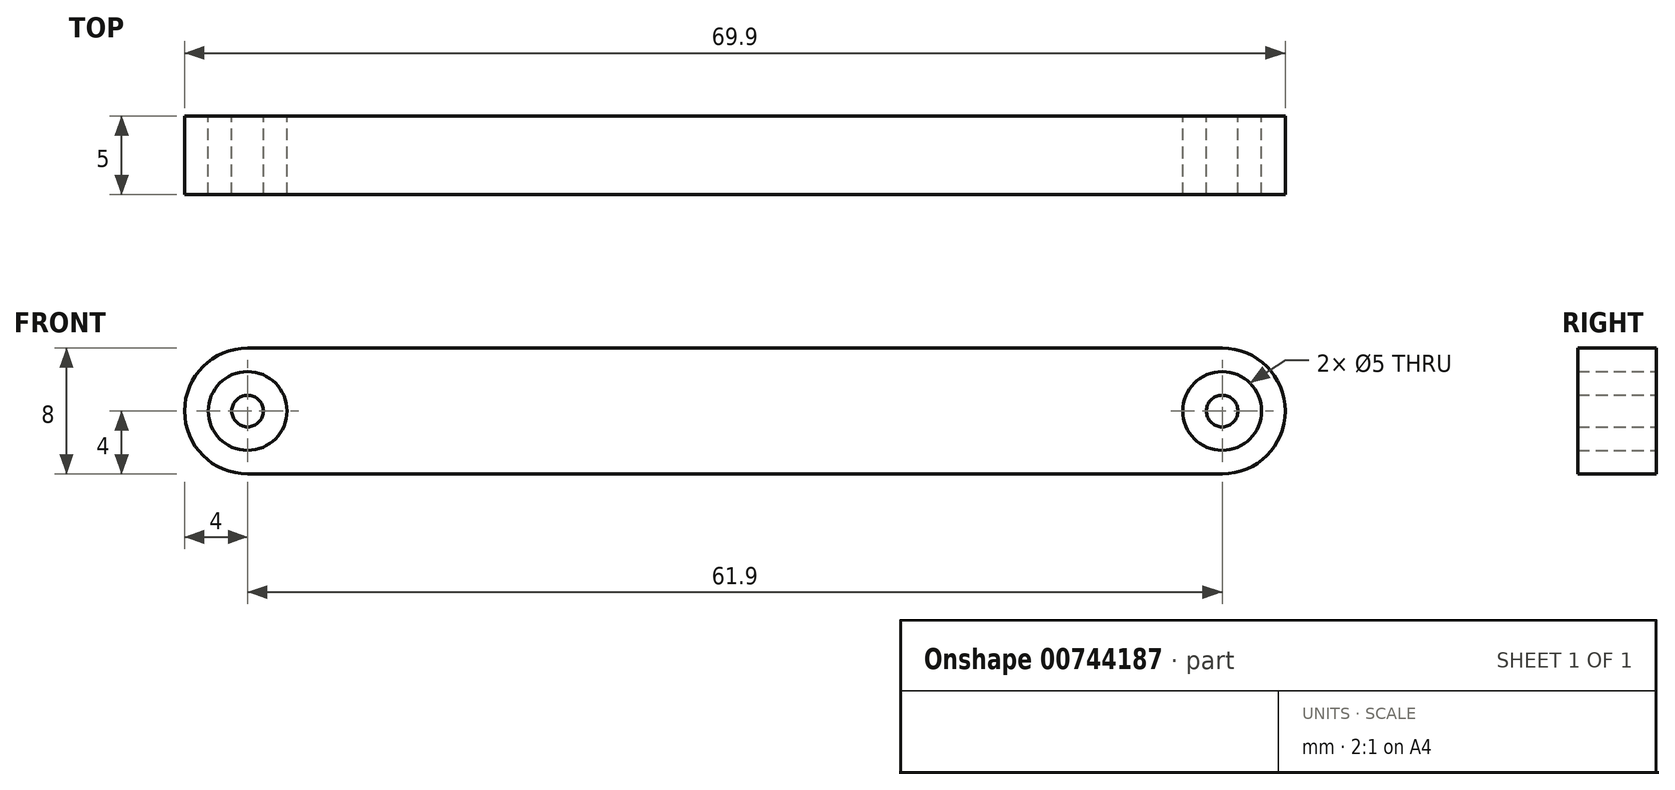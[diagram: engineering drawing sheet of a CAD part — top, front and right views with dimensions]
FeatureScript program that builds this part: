
annotation { "Feature Type Name" : "Feature", "Feature Type Description" : "" }
export const myFeature = defineFeature(function(context is Context, id is Id, definition is map)
    precondition{}
    {
        {
            var Q0;
            Q0=qCreatedBy(makeId("Front.planeOp"),FACE);
            var sketch = newSketch(context, id + "F0", { "sketchPlane" : qUnion([Q0])});
            skCircle(sketch, "E0", {"center": v(0, 0) * mm, "radius": 2.5 * mm});
            skCircle(sketch, "E1", {"center": v(0, 0) * mm, "radius": 1 * mm});
            skCircle(sketch, "E2", {"center": v(0, 0) * mm, "radius": 4 * mm});
            skCircle(sketch, "E3", {"center": v(61.9, 0) * mm, "radius": 4 * mm});
            skCircle(sketch, "E4", {"center": v(61.9, 0) * mm, "radius": 2.5 * mm});
            skCircle(sketch, "E5", {"center": v(61.9, 0) * mm, "radius": 1 * mm});
            skLineSegment(sketch, "E6", {"start": v(0, -4) * mm, "end": v(61.9, -4) * mm});
            skLineSegment(sketch, "E7", {"start": v(0, 4) * mm, "end": v(61.9, 4) * mm});
            skSolve(sketch);
        }
        {
            var Q0;
            Q0=qSketchRegion(id+"F0",true);
            var Q1;
            Q1=makeQuery(id+"F0.imprint","IMPRINT",FACE,{"disambiguationData":[TD([[makeQuery(id+"F0.imprint","IMPRINT",EDGE,{"derivedFrom":sQuery(id+"F0.wireOp",EDGE,"E1")}),1.0]])]});
            var Q2;
            Q2=makeQuery(id+"F0.imprint","IMPRINT",FACE,{"disambiguationData":[TD([[makeQuery(id+"F0.imprint","IMPRINT",EDGE,{"derivedFrom":sQuery(id+"F0.wireOp",EDGE,"E5")}),1.0]])]});
            extrude(context, id + "F1", {"entities" : qUnion([Q0, Q1, Q2]), "depth" : 5 * mm, "offsetDistance" : 25.4 * mm});
        }
    });
